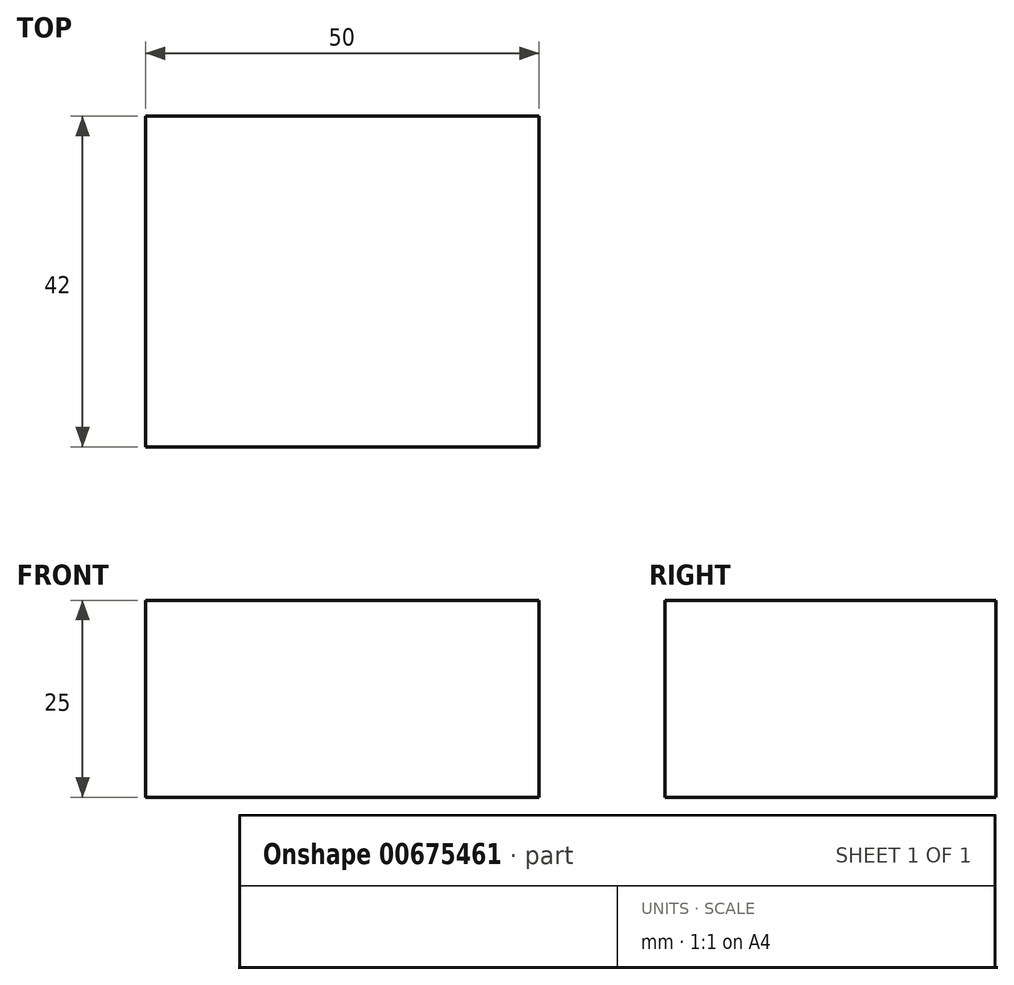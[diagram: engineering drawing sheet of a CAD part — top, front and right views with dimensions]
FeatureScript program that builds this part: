
annotation { "Feature Type Name" : "Feature", "Feature Type Description" : "" }
export const myFeature = defineFeature(function(context is Context, id is Id, definition is map)
    precondition{}
    {
        {
            var Q0;
            Q0=qCreatedBy(makeId("Top.planeOp"),FACE);
            var sketch = newSketch(context, id + "F0", { "sketchPlane" : qUnion([Q0])});
            skLineSegment(sketch, "E0", {"start": v(-29.2, 20.83) * mm, "end": v(20.8, 20.83) * mm});
            skLineSegment(sketch, "E1", {"start": v(20.8, -21.17) * mm, "end": v(-29.2, -21.17) * mm});
            skLineSegment(sketch, "E2", {"start": v(-29.2, -21.17) * mm, "end": v(-29.2, 20.83) * mm});
            skLineSegment(sketch, "E3", {"start": v(20.8, 20.83) * mm, "end": v(20.8, -21.17) * mm});
            skSolve(sketch);
        }
        {
            var Q0;
            Q0=makeQuery(id+"F0.imprint","IMPRINT",FACE,{"disambiguationData":[TD([[makeQuery(id+"F0.imprint","IMPRINT",EDGE,{"derivedFrom":sQuery(id+"F0.wireOp",EDGE,"E0")}),-1.0]])]});
            extrude(context, id + "F1", {"entities" : qUnion([Q0]), "depth" : 25 * mm, "offsetDistance" : 25 * mm});
        }
    });
